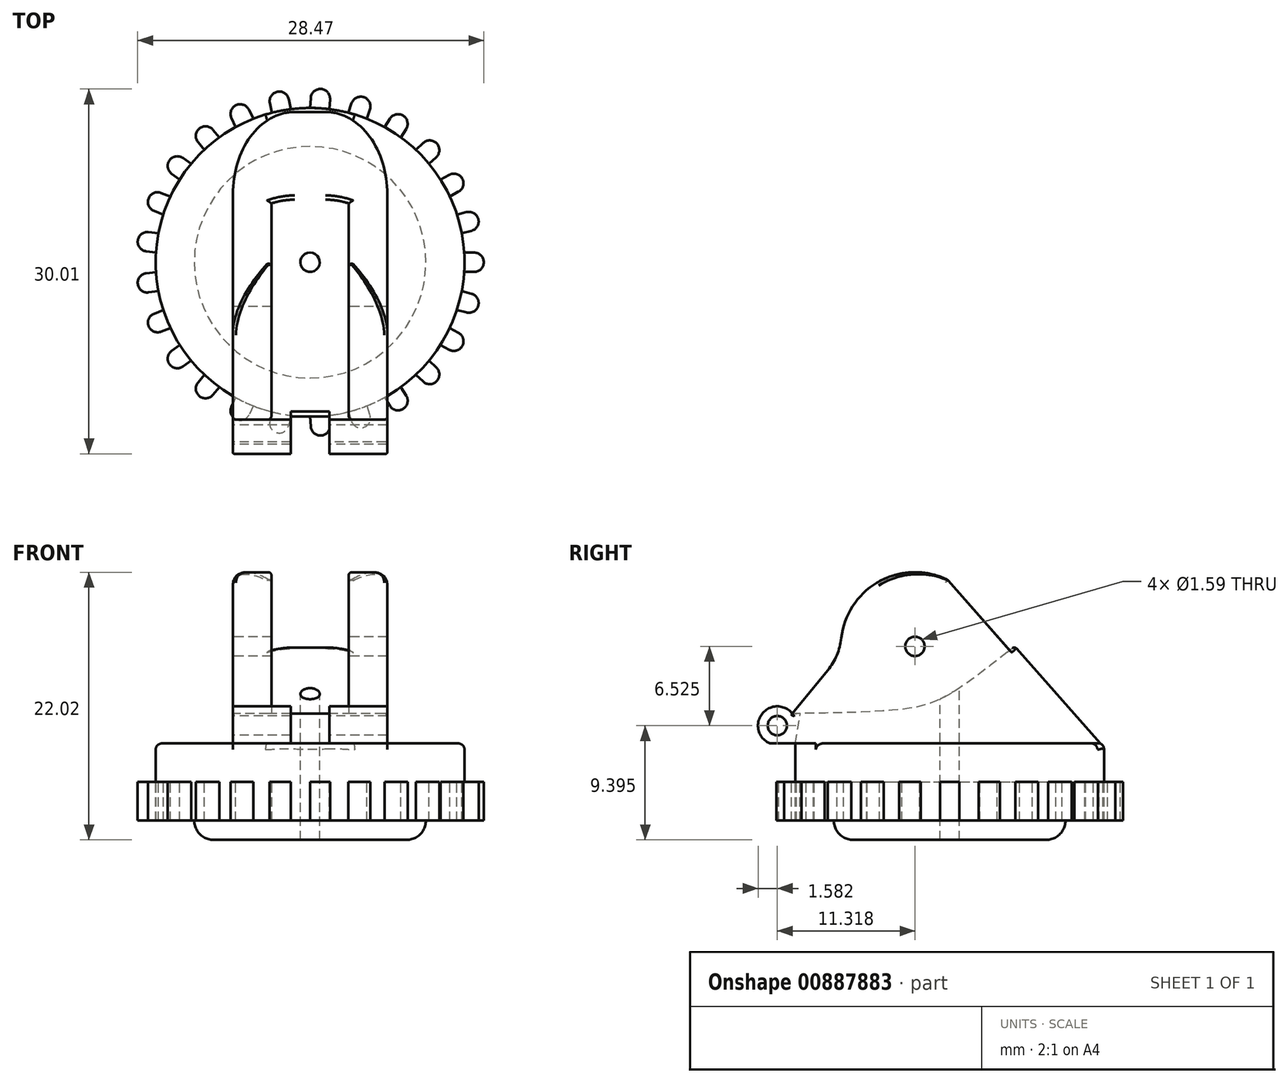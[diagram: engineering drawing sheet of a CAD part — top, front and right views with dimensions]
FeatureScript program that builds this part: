
annotation { "Feature Type Name" : "Feature", "Feature Type Description" : "" }
export const myFeature = defineFeature(function(context is Context, id is Id, definition is map)
    precondition{}
    {
        {
            var Q0;
            Q0=qCreatedBy(makeId("Right.planeOp"),FACE);
            var sketch = newSketch(context, id + "F0", { "sketchPlane" : qUnion([Q0])});
            skArc(sketch, "E0", {"start": v(4.53, 4.07) * mm, "mid": v(-2.46, 5.58) * mm, "end": v(-6.07, -0.6) * mm});
            skLineSegment(sketch, "E1", {"start": v(-6.07, -0.6) * mm, "end": v(-10.08, -5.53) * mm});
            skArc(sketch, "E2", {"start": v(-10.08, -5.53) * mm, "mid": v(-12.58, -5.57) * mm, "end": v(-11.94, -7.98) * mm});
            skCircle(sketch, "E3", {"center": v(0, 0) * mm, "radius": 0.8 * mm});
            skCircle(sketch, "E4", {"center": v(-11.32, -6.53) * mm, "radius": 0.8 * mm});
            skLineSegment(sketch, "E5", {"start": v(4.53, 4.07) * mm, "end": v(8.2, 0) * mm});
            skLineSegment(sketch, "E6", {"start": v(8.2, 0) * mm, "end": v(8.2, -7.98) * mm});
            skLineSegment(sketch, "E7", {"start": v(8.2, -7.98) * mm, "end": v(-11.94, -7.98) * mm});
            skPoint(sketch, "E8.end.orphan", {"position": v(0, -7.36) * mm});
            skFitSpline(sketch, "E9", {"points": [v(8.2, 0) * mm, v(2.56, -4.09) * mm, v(-1.11, -5.18) * mm, v(-10.08, -5.53) * mm], "startDerivative": vector(-17.3, -13.81) * mm, "endDerivative": vector(-25.55, -0.3) * mm});
            skLineSegment(sketch, "E10", {"start": v(-9.85, -7.98) * mm, "end": v(-9.42, -5.52) * mm});
            skLineSegment(sketch, "E11", {"start": v(8.2, 0) * mm, "end": v(15.23, -7.98) * mm});
            skLineSegment(sketch, "E12", {"start": v(15.23, -7.98) * mm, "end": v(8.2, -7.98) * mm});
            skSolve(sketch);
        }
        {
            var Q0;
            Q0=makeQuery(id+"F0.imprint","IMPRINT",FACE,{"disambiguationData":[TD([[makeQuery(id+"F0.imprint","IMPRINT",EDGE,{"derivedFrom":sQuery(id+"F0.wireOp",EDGE,"E0")}),1.0]])]});
            var Q1;
            {var subQ0=sQuery(id+"F0.wireOp",EDGE,"E6");Q1=makeQuery(id+"F0.imprint","IMPRINT",FACE,{"disambiguationData":[TD([[makeQuery(id+"F0.imprint","IMPRINT",EDGE,{"derivedFrom":subQ0}),-1.0]])]});}
            var Q2;
            {var subQ1=sQuery(id+"F0.wireOp",EDGE,"E2");Q2=makeQuery(id+"F0.imprint","IMPRINT",FACE,{"disambiguationData":[TD([[makeQuery(id+"F0.imprint","IMPRINT",EDGE,{"derivedFrom":subQ1}),1.0]])]});}
            extrude(context, id + "F1", {"entities" : qUnion([Q0, Q1, Q2]), "depth" : 12.7 * mm, "offsetDistance" : 25.4 * mm, "symmetric" : true});
        }
        {
            var Q0;
            Q0=makeQuery(id+"F0.imprint","IMPRINT",FACE,{"disambiguationData":[TD([[makeQuery(id+"F0.imprint","IMPRINT",EDGE,{"derivedFrom":sQuery(id+"F0.wireOp",EDGE,"E0")}),1.0]])]});
            extrude(context, id + "F2", {"entities" : qUnion([Q0]), "operationType" : NewBodyOperationType.REMOVE, "depth" : 6.35 * mm, "offsetDistance" : 25.4 * mm, "symmetric" : true});
        }
        {
            var Q0;
            {var subQ1=sQuery(id+"F0.wireOp",EDGE,"E2");Q0=makeQuery(id+"F0.imprint","IMPRINT",FACE,{"disambiguationData":[TD([[makeQuery(id+"F0.imprint","IMPRINT",EDGE,{"derivedFrom":subQ1}),1.0]])]});}
            extrude(context, id + "F3", {"entities" : qUnion([Q0]), "operationType" : NewBodyOperationType.REMOVE, "depth" : 3.17 * mm, "offsetDistance" : 25.4 * mm, "symmetric" : true});
        }
        {
            var Q0;
            Q0=makeQuery(id+"F1.opExtrude","SWEPT_FACE",FACE,{"disambiguationData":[OSD([sQuery(id+"F0.wireOp",EDGE,"E7")])]});
            var sketch = newSketch(context, id + "F4", { "sketchPlane" : qUnion([Q0])});
            skCircle(sketch, "E13", {"center": v(0, -2.85) * mm, "radius": 12.7 * mm});
            skPoint(sketch, "E13.centerSnap0", {"position": v(0, 9.85) * mm});
            skSolve(sketch);
        }
        {
            var Q0;
            {var subQ0=sQuery(id+"F0.wireOp",EDGE,"E7");var subQ2=makeQuery(id+"F1.opExtrude","SWEPT_EDGE",EDGE,{"disambiguationData":[OSD([sQuery(id+"F0.wireOp",EDGE,"E6"),subQ0])]});Q0=makeQuery(id+"F4.imprint","IMPRINT",FACE,{"disambiguationData":[TD([[makeQuery(id+"F4.imprint","IMPRINT",EDGE,{"derivedFrom":subQ2}),-1.0]])]});}
            var Q1;
            {var subQ1=sQuery(id+"F0.wireOp",EDGE,"E7");var subQ6=makeQuery(id+"F1.opExtrude","SWEPT_EDGE",EDGE,{"disambiguationData":[OSD([sQuery(id+"F0.wireOp",EDGE,"E6"),subQ1])]});Q1=makeQuery(id+"F4.imprint","IMPRINT",FACE,{"disambiguationData":[TD([[makeQuery(id+"F4.imprint","IMPRINT",EDGE,{"derivedFrom":subQ6}),1.0]])]});}
            extrude(context, id + "F5", {"entities" : qUnion([Q0, Q1]), "operationType" : NewBodyOperationType.ADD, "depth" : 3.17 * mm, "offsetDistance" : 25.4 * mm});
        }
        {
            var Q0;
            Q0=makeQuery(id+"F5.opExtrude","CAP_FACE",FACE,{"disambiguationData":[OSD([sQuery(id+"F4.wireOp",EDGE,"E13")])],"isStart":false});
            var sketch = newSketch(context, id + "F6", { "sketchPlane" : qUnion([Q0])});
            skCircle(sketch, "E14", {"center": v(0, -2.85) * mm, "radius": 12.7 * mm});
            skLineSegment(sketch, "E15", {"start": v(12.68, -2.06) * mm, "end": v(13.5, -2.06) * mm});
            skLineSegment(sketch, "E16", {"start": v(12.68, -3.65) * mm, "end": v(13.5, -3.65) * mm});
            skLineSegment(sketch, "E17", {"start": v(14.29, -2.85) * mm, "end": v(14.29, -2.85) * mm});
            skPoint(sketch, "E18.end.orphan", {"position": v(14.29, -2.85) * mm});
            skArc(sketch, "E19.filletArc", {"start": v(14.29, -2.85) * mm, "mid": v(14.06, -2.3) * mm, "end": v(13.5, -2.06) * mm});
            skArc(sketch, "E20.filletArc", {"start": v(13.5, -3.65) * mm, "mid": v(14.06, -3.42) * mm, "end": v(14.29, -2.85) * mm});
            skLineSegment(sketch, "E21.1.0", {"start": v(12.08, 1.07) * mm, "end": v(12.87, 1.27) * mm});
            skArc(sketch, "E21.1.1", {"start": v(13.84, 0.7) * mm, "mid": v(13.47, 1.18) * mm, "end": v(12.87, 1.27) * mm});
            skArc(sketch, "E21.1.2", {"start": v(13.27, -0.27) * mm, "mid": v(13.75, 0.1) * mm, "end": v(13.84, 0.7) * mm});
            skLineSegment(sketch, "E21.1.3", {"start": v(12.47, -0.47) * mm, "end": v(13.27, -0.27) * mm});
            skLineSegment(sketch, "E21.2.0", {"start": v(10.72, 3.95) * mm, "end": v(11.44, 4.34) * mm});
            skArc(sketch, "E21.2.1", {"start": v(12.52, 4.03) * mm, "mid": v(12.05, 4.4) * mm, "end": v(11.44, 4.34) * mm});
            skArc(sketch, "E21.2.2", {"start": v(12.2, 2.95) * mm, "mid": v(12.59, 3.43) * mm, "end": v(12.52, 4.03) * mm});
            skLineSegment(sketch, "E21.2.3", {"start": v(11.49, 2.56) * mm, "end": v(12.2, 2.95) * mm});
            skLineSegment(sketch, "E21.3.0", {"start": v(8.7, 6.4) * mm, "end": v(9.3, 6.96) * mm});
            skArc(sketch, "E21.3.1", {"start": v(10.42, 6.93) * mm, "mid": v(9.86, 7.18) * mm, "end": v(9.3, 6.96) * mm});
            skArc(sketch, "E21.3.2", {"start": v(10.38, 5.8) * mm, "mid": v(10.63, 6.36) * mm, "end": v(10.42, 6.93) * mm});
            skLineSegment(sketch, "E21.3.3", {"start": v(9.78, 5.24) * mm, "end": v(10.38, 5.8) * mm});
            skLineSegment(sketch, "E21.4.0", {"start": v(6.12, 8.27) * mm, "end": v(6.56, 8.96) * mm});
            skArc(sketch, "E21.4.1", {"start": v(7.66, 9.2) * mm, "mid": v(7.06, 9.31) * mm, "end": v(6.56, 8.96) * mm});
            skArc(sketch, "E21.4.2", {"start": v(7.9, 8.11) * mm, "mid": v(8, 8.71) * mm, "end": v(7.66, 9.2) * mm});
            skLineSegment(sketch, "E21.4.3", {"start": v(7.46, 7.42) * mm, "end": v(7.9, 8.11) * mm});
            skLineSegment(sketch, "E21.5.0", {"start": v(3.16, 9.45) * mm, "end": v(3.41, 10.22) * mm});
            skArc(sketch, "E21.5.1", {"start": v(4.42, 10.73) * mm, "mid": v(3.8, 10.69) * mm, "end": v(3.41, 10.22) * mm});
            skArc(sketch, "E21.5.2", {"start": v(4.92, 9.73) * mm, "mid": v(4.88, 10.34) * mm, "end": v(4.42, 10.73) * mm});
            skLineSegment(sketch, "E21.5.3", {"start": v(4.67, 8.96) * mm, "end": v(4.92, 9.73) * mm});
            skLineSegment(sketch, "E21.6.0", {"start": v(0, 9.85) * mm, "end": v(0.06, 10.66) * mm});
            skArc(sketch, "E21.6.1", {"start": v(0.9, 11.4) * mm, "mid": v(0.32, 11.2) * mm, "end": v(0.06, 10.66) * mm});
            skArc(sketch, "E21.6.2", {"start": v(1.64, 10.56) * mm, "mid": v(1.44, 11.14) * mm, "end": v(0.9, 11.4) * mm});
            skLineSegment(sketch, "E21.6.3", {"start": v(1.59, 9.75) * mm, "end": v(1.64, 10.56) * mm});
            skLineSegment(sketch, "E21.7.0", {"start": v(-3.15, 9.45) * mm, "end": v(-3.3, 10.25) * mm});
            skArc(sketch, "E21.7.1", {"start": v(-2.68, 11.18) * mm, "mid": v(-3.18, 10.85) * mm, "end": v(-3.3, 10.25) * mm});
            skArc(sketch, "E21.7.2", {"start": v(-1.75, 10.55) * mm, "mid": v(-2.08, 11.06) * mm, "end": v(-2.68, 11.18) * mm});
            skLineSegment(sketch, "E21.7.3", {"start": v(-1.6, 9.75) * mm, "end": v(-1.75, 10.55) * mm});
            skLineSegment(sketch, "E21.8.0", {"start": v(-6.12, 8.28) * mm, "end": v(-6.46, 9.02) * mm});
            skArc(sketch, "E21.8.1", {"start": v(-6.08, 10.07) * mm, "mid": v(-6.5, 9.62) * mm, "end": v(-6.46, 9.02) * mm});
            skArc(sketch, "E21.8.2", {"start": v(-5.03, 9.7) * mm, "mid": v(-5.48, 10.1) * mm, "end": v(-6.08, 10.07) * mm});
            skLineSegment(sketch, "E21.8.3", {"start": v(-4.68, 8.95) * mm, "end": v(-5.03, 9.7) * mm});
            skLineSegment(sketch, "E21.9.0", {"start": v(-8.7, 6.4) * mm, "end": v(-9.21, 7.04) * mm});
            skArc(sketch, "E21.9.1", {"start": v(-9.1, 8.15) * mm, "mid": v(-9.4, 7.62) * mm, "end": v(-9.21, 7.04) * mm});
            skArc(sketch, "E21.9.2", {"start": v(-7.99, 8.05) * mm, "mid": v(-8.53, 8.33) * mm, "end": v(-9.1, 8.15) * mm});
            skLineSegment(sketch, "E21.9.3", {"start": v(-7.47, 7.42) * mm, "end": v(-7.99, 8.05) * mm});
            skLineSegment(sketch, "E21.10.0", {"start": v(-10.72, 3.95) * mm, "end": v(-11.38, 4.44) * mm});
            skArc(sketch, "E21.10.1", {"start": v(-11.56, 5.54) * mm, "mid": v(-11.7, 4.95) * mm, "end": v(-11.38, 4.44) * mm});
            skArc(sketch, "E21.10.2", {"start": v(-10.45, 5.72) * mm, "mid": v(-11.04, 5.86) * mm, "end": v(-11.56, 5.54) * mm});
            skLineSegment(sketch, "E21.10.3", {"start": v(-9.79, 5.24) * mm, "end": v(-10.45, 5.72) * mm});
            skLineSegment(sketch, "E21.11.0", {"start": v(-12.08, 1.07) * mm, "end": v(-12.84, 1.38) * mm});
            skArc(sketch, "E21.11.1", {"start": v(-13.28, 2.4) * mm, "mid": v(-13.27, 1.8) * mm, "end": v(-12.84, 1.38) * mm});
            skArc(sketch, "E21.11.2", {"start": v(-12.25, 2.85) * mm, "mid": v(-12.86, 2.84) * mm, "end": v(-13.28, 2.4) * mm});
            skLineSegment(sketch, "E21.11.3", {"start": v(-11.5, 2.55) * mm, "end": v(-12.25, 2.85) * mm});
            skLineSegment(sketch, "E21.12.0", {"start": v(-12.67, -2.05) * mm, "end": v(-13.49, -1.95) * mm});
            skArc(sketch, "E21.12.1", {"start": v(-14.17, -1.06) * mm, "mid": v(-14.01, -1.65) * mm, "end": v(-13.49, -1.95) * mm});
            skArc(sketch, "E21.12.2", {"start": v(-13.29, -0.38) * mm, "mid": v(-13.87, -0.54) * mm, "end": v(-14.17, -1.06) * mm});
            skLineSegment(sketch, "E21.12.3", {"start": v(-12.48, -0.48) * mm, "end": v(-13.29, -0.38) * mm});
            skLineSegment(sketch, "E21.13.0", {"start": v(-12.48, -5.23) * mm, "end": v(-13.29, -5.33) * mm});
            skArc(sketch, "E21.13.1", {"start": v(-14.17, -4.64) * mm, "mid": v(-13.87, -5.17) * mm, "end": v(-13.29, -5.33) * mm});
            skArc(sketch, "E21.13.2", {"start": v(-13.49, -3.76) * mm, "mid": v(-14.01, -4.06) * mm, "end": v(-14.17, -4.64) * mm});
            skLineSegment(sketch, "E21.13.3", {"start": v(-12.67, -3.66) * mm, "end": v(-13.49, -3.76) * mm});
            skLineSegment(sketch, "E21.14.0", {"start": v(-11.5, -8.26) * mm, "end": v(-12.25, -8.56) * mm});
            skArc(sketch, "E21.14.1", {"start": v(-13.28, -8.11) * mm, "mid": v(-12.86, -8.55) * mm, "end": v(-12.25, -8.56) * mm});
            skArc(sketch, "E21.14.2", {"start": v(-12.84, -7.08) * mm, "mid": v(-13.27, -7.5) * mm, "end": v(-13.28, -8.11) * mm});
            skLineSegment(sketch, "E21.14.3", {"start": v(-12.08, -6.78) * mm, "end": v(-12.84, -7.08) * mm});
            skLineSegment(sketch, "E21.15.0", {"start": v(-9.79, -10.95) * mm, "end": v(-10.45, -11.43) * mm});
            skArc(sketch, "E21.15.1", {"start": v(-11.56, -11.25) * mm, "mid": v(-11.04, -11.57) * mm, "end": v(-10.45, -11.43) * mm});
            skArc(sketch, "E21.15.2", {"start": v(-11.38, -10.14) * mm, "mid": v(-11.7, -10.66) * mm, "end": v(-11.56, -11.25) * mm});
            skLineSegment(sketch, "E21.15.3", {"start": v(-10.72, -9.66) * mm, "end": v(-11.38, -10.14) * mm});
            skLineSegment(sketch, "E21.16.0", {"start": v(-7.47, -13.13) * mm, "end": v(-7.99, -13.76) * mm});
            skArc(sketch, "E21.16.1", {"start": v(-9.1, -13.86) * mm, "mid": v(-8.53, -14.04) * mm, "end": v(-7.99, -13.76) * mm});
            skArc(sketch, "E21.16.2", {"start": v(-9.21, -12.75) * mm, "mid": v(-9.4, -13.33) * mm, "end": v(-9.1, -13.86) * mm});
            skLineSegment(sketch, "E21.16.3", {"start": v(-8.7, -12.11) * mm, "end": v(-9.21, -12.75) * mm});
            skLineSegment(sketch, "E21.17.0", {"start": v(-4.68, -14.66) * mm, "end": v(-5.03, -15.4) * mm});
            skArc(sketch, "E21.17.1", {"start": v(-6.08, -15.78) * mm, "mid": v(-5.48, -15.81) * mm, "end": v(-5.03, -15.4) * mm});
            skArc(sketch, "E21.17.2", {"start": v(-6.46, -14.73) * mm, "mid": v(-6.5, -15.33) * mm, "end": v(-6.08, -15.78) * mm});
            skLineSegment(sketch, "E21.17.3", {"start": v(-6.12, -13.98) * mm, "end": v(-6.46, -14.73) * mm});
            skLineSegment(sketch, "E21.18.0", {"start": v(-1.6, -15.45) * mm, "end": v(-1.75, -16.26) * mm});
            skArc(sketch, "E21.18.1", {"start": v(-2.68, -16.89) * mm, "mid": v(-2.08, -16.77) * mm, "end": v(-1.75, -16.26) * mm});
            skArc(sketch, "E21.18.2", {"start": v(-3.3, -15.96) * mm, "mid": v(-3.18, -16.55) * mm, "end": v(-2.68, -16.89) * mm});
            skLineSegment(sketch, "E21.18.3", {"start": v(-3.15, -15.16) * mm, "end": v(-3.3, -15.96) * mm});
            skLineSegment(sketch, "E21.19.0", {"start": v(1.59, -15.45) * mm, "end": v(1.64, -16.27) * mm});
            skArc(sketch, "E21.19.1", {"start": v(0.9, -17.11) * mm, "mid": v(1.44, -16.85) * mm, "end": v(1.64, -16.27) * mm});
            skArc(sketch, "E21.19.2", {"start": v(0.06, -16.37) * mm, "mid": v(0.32, -16.92) * mm, "end": v(0.9, -17.11) * mm});
            skLineSegment(sketch, "E21.19.3", {"start": v(0, -15.55) * mm, "end": v(0.06, -16.37) * mm});
            skLineSegment(sketch, "E21.20.0", {"start": v(4.67, -14.66) * mm, "end": v(4.92, -15.44) * mm});
            skArc(sketch, "E21.20.1", {"start": v(4.42, -16.44) * mm, "mid": v(4.88, -16.05) * mm, "end": v(4.92, -15.44) * mm});
            skArc(sketch, "E21.20.2", {"start": v(3.41, -15.93) * mm, "mid": v(3.8, -16.4) * mm, "end": v(4.42, -16.44) * mm});
            skLineSegment(sketch, "E21.20.3", {"start": v(3.16, -15.15) * mm, "end": v(3.41, -15.93) * mm});
            skLineSegment(sketch, "E21.21.0", {"start": v(7.46, -13.13) * mm, "end": v(7.9, -13.82) * mm});
            skArc(sketch, "E21.21.1", {"start": v(7.66, -14.92) * mm, "mid": v(8, -14.42) * mm, "end": v(7.9, -13.82) * mm});
            skArc(sketch, "E21.21.2", {"start": v(6.56, -14.67) * mm, "mid": v(7.06, -15.02) * mm, "end": v(7.66, -14.92) * mm});
            skLineSegment(sketch, "E21.21.3", {"start": v(6.12, -13.98) * mm, "end": v(6.56, -14.67) * mm});
            skLineSegment(sketch, "E21.22.0", {"start": v(9.78, -10.95) * mm, "end": v(10.38, -11.51) * mm});
            skArc(sketch, "E21.22.1", {"start": v(10.42, -12.63) * mm, "mid": v(10.63, -12.07) * mm, "end": v(10.38, -11.51) * mm});
            skArc(sketch, "E21.22.2", {"start": v(9.3, -12.67) * mm, "mid": v(9.86, -12.88) * mm, "end": v(10.42, -12.63) * mm});
            skLineSegment(sketch, "E21.22.3", {"start": v(8.7, -12.1) * mm, "end": v(9.3, -12.67) * mm});
            skLineSegment(sketch, "E21.23.0", {"start": v(11.49, -8.26) * mm, "end": v(12.2, -8.66) * mm});
            skArc(sketch, "E21.23.1", {"start": v(12.52, -9.74) * mm, "mid": v(12.59, -9.13) * mm, "end": v(12.2, -8.66) * mm});
            skArc(sketch, "E21.23.2", {"start": v(11.44, -10.05) * mm, "mid": v(12.05, -10.12) * mm, "end": v(12.52, -9.74) * mm});
            skLineSegment(sketch, "E21.23.3", {"start": v(10.72, -9.66) * mm, "end": v(11.44, -10.05) * mm});
            skArc(sketch, "E22.3.24.0", {"start": v(13.84, -6.4) * mm, "mid": v(13.75, -5.8) * mm, "end": v(13.27, -5.44) * mm});
            skLineSegment(sketch, "E22.4.24.0", {"start": v(12.47, -5.24) * mm, "end": v(13.27, -5.44) * mm});
            skArc(sketch, "E22.7.24.0", {"start": v(12.87, -6.98) * mm, "mid": v(13.47, -6.9) * mm, "end": v(13.84, -6.4) * mm});
            skLineSegment(sketch, "E22.11.24.0", {"start": v(12.08, -6.77) * mm, "end": v(12.87, -6.98) * mm});
            skCircle(sketch, "E23", {"center": v(0, -2.85) * mm, "radius": 0.8 * mm});
            skCircle(sketch, "E24", {"center": v(0, -2.85) * mm, "radius": 9.53 * mm});
            skSolve(sketch);
        }
        {
            var Q0;
            {var subQ0=sQuery(id+"F6.wireOp",EDGE,"E21.18.0");Q0=makeQuery(id+"F6.imprint","IMPRINT",FACE,{"disambiguationData":[TD([[makeQuery(id+"F6.imprint","IMPRINT",EDGE,{"derivedFrom":subQ0}),-1.0]])]});}
            var Q1;
            {var subQ0=sQuery(id+"F6.wireOp",EDGE,"E21.17.0");Q1=makeQuery(id+"F6.imprint","IMPRINT",FACE,{"disambiguationData":[TD([[makeQuery(id+"F6.imprint","IMPRINT",EDGE,{"derivedFrom":subQ0}),-1.0]])]});}
            var Q2;
            {var subQ0=sQuery(id+"F6.wireOp",EDGE,"E21.16.0");Q2=makeQuery(id+"F6.imprint","IMPRINT",FACE,{"disambiguationData":[TD([[makeQuery(id+"F6.imprint","IMPRINT",EDGE,{"derivedFrom":subQ0}),-1.0]])]});}
            var Q3;
            {var subQ0=sQuery(id+"F6.wireOp",EDGE,"E21.15.0");Q3=makeQuery(id+"F6.imprint","IMPRINT",FACE,{"disambiguationData":[TD([[makeQuery(id+"F6.imprint","IMPRINT",EDGE,{"derivedFrom":subQ0}),-1.0]])]});}
            var Q4;
            {var subQ0=sQuery(id+"F6.wireOp",EDGE,"E21.14.0");Q4=makeQuery(id+"F6.imprint","IMPRINT",FACE,{"disambiguationData":[TD([[makeQuery(id+"F6.imprint","IMPRINT",EDGE,{"derivedFrom":subQ0}),-1.0]])]});}
            var Q5;
            Q5=makeQuery(id+"F6.imprint","IMPRINT",FACE,{"disambiguationData":[TD([[makeQuery(id+"F6.imprint","IMPRINT",EDGE,{"derivedFrom":sQuery(id+"F6.wireOp",EDGE,"E24")}),-1.0]])]});
            var Q6;
            {var subQ0=sQuery(id+"F6.wireOp",EDGE,"E21.13.0");Q6=makeQuery(id+"F6.imprint","IMPRINT",FACE,{"disambiguationData":[TD([[makeQuery(id+"F6.imprint","IMPRINT",EDGE,{"derivedFrom":subQ0}),-1.0]])]});}
            var Q7;
            {var subQ0=sQuery(id+"F6.wireOp",EDGE,"E21.12.0");Q7=makeQuery(id+"F6.imprint","IMPRINT",FACE,{"disambiguationData":[TD([[makeQuery(id+"F6.imprint","IMPRINT",EDGE,{"derivedFrom":subQ0}),-1.0]])]});}
            var Q8;
            {var subQ0=sQuery(id+"F6.wireOp",EDGE,"E21.11.0");Q8=makeQuery(id+"F6.imprint","IMPRINT",FACE,{"disambiguationData":[TD([[makeQuery(id+"F6.imprint","IMPRINT",EDGE,{"derivedFrom":subQ0}),-1.0]])]});}
            var Q9;
            {var subQ0=sQuery(id+"F6.wireOp",EDGE,"E21.10.0");Q9=makeQuery(id+"F6.imprint","IMPRINT",FACE,{"disambiguationData":[TD([[makeQuery(id+"F6.imprint","IMPRINT",EDGE,{"derivedFrom":subQ0}),-1.0]])]});}
            var Q10;
            {var subQ0=sQuery(id+"F6.wireOp",EDGE,"E21.9.0");Q10=makeQuery(id+"F6.imprint","IMPRINT",FACE,{"disambiguationData":[TD([[makeQuery(id+"F6.imprint","IMPRINT",EDGE,{"derivedFrom":subQ0}),-1.0]])]});}
            var Q11;
            {var subQ0=sQuery(id+"F6.wireOp",EDGE,"E21.8.0");Q11=makeQuery(id+"F6.imprint","IMPRINT",FACE,{"disambiguationData":[TD([[makeQuery(id+"F6.imprint","IMPRINT",EDGE,{"derivedFrom":subQ0}),-1.0]])]});}
            var Q12;
            {var subQ0=sQuery(id+"F6.wireOp",EDGE,"E21.7.0");Q12=makeQuery(id+"F6.imprint","IMPRINT",FACE,{"disambiguationData":[TD([[makeQuery(id+"F6.imprint","IMPRINT",EDGE,{"derivedFrom":subQ0}),-1.0]])]});}
            var Q13;
            {var subQ0=sQuery(id+"F6.wireOp",EDGE,"E21.6.0");Q13=makeQuery(id+"F6.imprint","IMPRINT",FACE,{"disambiguationData":[TD([[makeQuery(id+"F6.imprint","IMPRINT",EDGE,{"derivedFrom":subQ0}),-1.0]])]});}
            var Q14;
            {var subQ0=sQuery(id+"F6.wireOp",EDGE,"E21.5.0");Q14=makeQuery(id+"F6.imprint","IMPRINT",FACE,{"disambiguationData":[TD([[makeQuery(id+"F6.imprint","IMPRINT",EDGE,{"derivedFrom":subQ0}),-1.0]])]});}
            var Q15;
            {var subQ0=sQuery(id+"F6.wireOp",EDGE,"E21.4.0");Q15=makeQuery(id+"F6.imprint","IMPRINT",FACE,{"disambiguationData":[TD([[makeQuery(id+"F6.imprint","IMPRINT",EDGE,{"derivedFrom":subQ0}),-1.0]])]});}
            var Q16;
            {var subQ0=sQuery(id+"F6.wireOp",EDGE,"E21.3.0");Q16=makeQuery(id+"F6.imprint","IMPRINT",FACE,{"disambiguationData":[TD([[makeQuery(id+"F6.imprint","IMPRINT",EDGE,{"derivedFrom":subQ0}),-1.0]])]});}
            var Q17;
            {var subQ0=sQuery(id+"F6.wireOp",EDGE,"E21.2.0");Q17=makeQuery(id+"F6.imprint","IMPRINT",FACE,{"disambiguationData":[TD([[makeQuery(id+"F6.imprint","IMPRINT",EDGE,{"derivedFrom":subQ0}),-1.0]])]});}
            var Q18;
            {var subQ0=sQuery(id+"F6.wireOp",EDGE,"E21.1.0");Q18=makeQuery(id+"F6.imprint","IMPRINT",FACE,{"disambiguationData":[TD([[makeQuery(id+"F6.imprint","IMPRINT",EDGE,{"derivedFrom":subQ0}),-1.0]])]});}
            var Q19;
            {var subQ1=sQuery(id+"F6.wireOp",EDGE,"E15");Q19=makeQuery(id+"F6.imprint","IMPRINT",FACE,{"disambiguationData":[TD([[makeQuery(id+"F6.imprint","IMPRINT",EDGE,{"derivedFrom":subQ1}),-1.0]])]});}
            var Q20;
            Q20=makeQuery(id+"F6.imprint","IMPRINT",FACE,{"disambiguationData":[TD([[makeQuery(id+"F6.imprint","IMPRINT",EDGE,{"derivedFrom":sQuery(id+"F6.wireOp",EDGE,"E22.3.24.0")}),1.0]])]});
            var Q21;
            {var subQ0=sQuery(id+"F6.wireOp",EDGE,"E21.23.0");Q21=makeQuery(id+"F6.imprint","IMPRINT",FACE,{"disambiguationData":[TD([[makeQuery(id+"F6.imprint","IMPRINT",EDGE,{"derivedFrom":subQ0}),-1.0]])]});}
            var Q22;
            {var subQ0=sQuery(id+"F6.wireOp",EDGE,"E21.22.0");Q22=makeQuery(id+"F6.imprint","IMPRINT",FACE,{"disambiguationData":[TD([[makeQuery(id+"F6.imprint","IMPRINT",EDGE,{"derivedFrom":subQ0}),-1.0]])]});}
            var Q23;
            {var subQ0=sQuery(id+"F6.wireOp",EDGE,"E21.20.0");Q23=makeQuery(id+"F6.imprint","IMPRINT",FACE,{"disambiguationData":[TD([[makeQuery(id+"F6.imprint","IMPRINT",EDGE,{"derivedFrom":subQ0}),-1.0]])]});}
            var Q24;
            {var subQ0=sQuery(id+"F6.wireOp",EDGE,"E21.21.0");Q24=makeQuery(id+"F6.imprint","IMPRINT",FACE,{"disambiguationData":[TD([[makeQuery(id+"F6.imprint","IMPRINT",EDGE,{"derivedFrom":subQ0}),-1.0]])]});}
            var Q25;
            {var subQ0=sQuery(id+"F6.wireOp",EDGE,"E21.19.0");Q25=makeQuery(id+"F6.imprint","IMPRINT",FACE,{"disambiguationData":[TD([[makeQuery(id+"F6.imprint","IMPRINT",EDGE,{"derivedFrom":subQ0}),-1.0]])]});}
            extrude(context, id + "F7", {"entities" : qUnion([Q0, Q1, Q2, Q3, Q4, Q5, Q6, Q7, Q8, Q9, Q10, Q11, Q12, Q13, Q14, Q15, Q16, Q17, Q18, Q19, Q20, Q21, Q22, Q23, Q24, Q25]), "operationType" : NewBodyOperationType.ADD, "depth" : 3.17 * mm, "offsetDistance" : 25.4 * mm});
        }
        {
            var Q0;
            Q0=makeQuery(id+"F6.imprint","IMPRINT",FACE,{"disambiguationData":[TD([[makeQuery(id+"F6.imprint","IMPRINT",EDGE,{"derivedFrom":sQuery(id+"F6.wireOp",EDGE,"E23")}),-1.0]])]});
            extrude(context, id + "F8", {"entities" : qUnion([Q0]), "operationType" : NewBodyOperationType.ADD, "depth" : 4.76 * mm, "offsetDistance" : 25.4 * mm});
        }
        {
            var Q0;
            Q0=makeQuery(id+"F6.imprint","IMPRINT",FACE,{"disambiguationData":[TD([[makeQuery(id+"F6.imprint","IMPRINT",EDGE,{"derivedFrom":sQuery(id+"F6.wireOp",EDGE,"E23")}),1.0]])]});
            extrude(context, id + "F9", {"entities" : qUnion([Q0]), "operationType" : NewBodyOperationType.REMOVE, "oppositeDirection" : true, "depth" : 25.4 * mm, "offsetDistance" : 25.4 * mm});
        }
        {
            var Q0;
            Q0=makeQuery(id+"F0.imprint","IMPRINT",FACE,{"disambiguationData":[TD([[makeQuery(id+"F0.imprint","IMPRINT",EDGE,{"derivedFrom":sQuery(id+"F0.wireOp",EDGE,"E6")}),1.0]])]});
            extrude(context, id + "F10", {"entities" : qUnion([Q0]), "operationType" : NewBodyOperationType.ADD, "depth" : 12.7 * mm, "offsetDistance" : 25.4 * mm, "symmetric" : true});
        }
        {
            var Q0;
            Q0=makeQuery(id+"F10.opExtrude","CAP_EDGE",EDGE,{"disambiguationData":[OSD([sQuery(id+"F0.wireOp",EDGE,"E11")])],"isStart":true});
            var Q1;
            Q1=makeQuery(id+"F10.opExtrude","CAP_EDGE",EDGE,{"disambiguationData":[OSD([sQuery(id+"F0.wireOp",EDGE,"E11")])],"isStart":false});
            fillet(context, id + "F11", {"entities" : qUnion([Q0, Q1]), "radius" : 5.08 * mm, "tangentPropagation" : true, "allowEdgeOverflow" : false});
        }
        {
            var Q0;
            {var subQ0=sQuery(id+"F6.wireOp",EDGE,"E14");var subQ1=makeQuery(id+"F7.opExtrude","SWEPT_FACE",FACE,{"disambiguationData":[OSD([subQ0]),TDD([makeQuery(id+"F6.imprint","IMPRINT",EDGE,{"disambiguationData":[TD([[makeQuery(id+"F6.imprint","INTERSECT",VERTEX,{"derivedFrom":[subQ0,sQuery(id+"F6.wireOp",EDGE,"E21.19.0")]}),-1.0]])],"derivedFrom":subQ0})])]});var subQ2=makeQuery(id+"F7.opExtrude","SWEPT_FACE",FACE,{"disambiguationData":[OSD([subQ0]),TDD([makeQuery(id+"F6.imprint","IMPRINT",EDGE,{"disambiguationData":[TD([[makeQuery(id+"F6.imprint","INTERSECT",VERTEX,{"derivedFrom":[subQ0,sQuery(id+"F6.wireOp",EDGE,"E21.18.0")]}),-1.0]])],"derivedFrom":subQ0})])]});var subQ3=makeQuery(id+"F7.opExtrude","SWEPT_FACE",FACE,{"disambiguationData":[OSD([subQ0]),TDD([makeQuery(id+"F6.imprint","IMPRINT",EDGE,{"disambiguationData":[TD([[makeQuery(id+"F6.imprint","INTERSECT",VERTEX,{"derivedFrom":[subQ0,sQuery(id+"F6.wireOp",EDGE,"E21.17.0")]}),-1.0]])],"derivedFrom":subQ0})])]});var subQ4=makeQuery(id+"F7.opExtrude","SWEPT_FACE",FACE,{"disambiguationData":[OSD([subQ0]),TDD([makeQuery(id+"F6.imprint","IMPRINT",EDGE,{"disambiguationData":[TD([[makeQuery(id+"F6.imprint","INTERSECT",VERTEX,{"derivedFrom":[subQ0,sQuery(id+"F6.wireOp",EDGE,"E21.16.0")]}),-1.0]])],"derivedFrom":subQ0})])]});var subQ5=makeQuery(id+"F7.opExtrude","SWEPT_FACE",FACE,{"disambiguationData":[OSD([subQ0]),TDD([makeQuery(id+"F6.imprint","IMPRINT",EDGE,{"disambiguationData":[TD([[makeQuery(id+"F6.imprint","INTERSECT",VERTEX,{"derivedFrom":[subQ0,sQuery(id+"F6.wireOp",EDGE,"E21.15.0")]}),-1.0]])],"derivedFrom":subQ0})])]});var subQ6=makeQuery(id+"F7.opExtrude","SWEPT_FACE",FACE,{"disambiguationData":[OSD([subQ0]),TDD([makeQuery(id+"F6.imprint","IMPRINT",EDGE,{"disambiguationData":[TD([[makeQuery(id+"F6.imprint","INTERSECT",VERTEX,{"derivedFrom":[subQ0,sQuery(id+"F6.wireOp",EDGE,"E21.14.0")]}),-1.0]])],"derivedFrom":subQ0})])]});var subQ7=makeQuery(id+"F7.opExtrude","SWEPT_FACE",FACE,{"disambiguationData":[OSD([subQ0]),TDD([makeQuery(id+"F6.imprint","IMPRINT",EDGE,{"disambiguationData":[TD([[makeQuery(id+"F6.imprint","INTERSECT",VERTEX,{"derivedFrom":[subQ0,sQuery(id+"F6.wireOp",EDGE,"E21.13.0")]}),-1.0]])],"derivedFrom":subQ0})])]});var subQ8=makeQuery(id+"F7.opExtrude","SWEPT_FACE",FACE,{"disambiguationData":[OSD([subQ0]),TDD([makeQuery(id+"F6.imprint","IMPRINT",EDGE,{"disambiguationData":[TD([[makeQuery(id+"F6.imprint","INTERSECT",VERTEX,{"derivedFrom":[subQ0,sQuery(id+"F6.wireOp",EDGE,"E21.12.0")]}),-1.0]])],"derivedFrom":subQ0})])]});var subQ9=makeQuery(id+"F7.opExtrude","SWEPT_FACE",FACE,{"disambiguationData":[OSD([subQ0]),TDD([makeQuery(id+"F6.imprint","IMPRINT",EDGE,{"disambiguationData":[TD([[makeQuery(id+"F6.imprint","INTERSECT",VERTEX,{"derivedFrom":[subQ0,sQuery(id+"F6.wireOp",EDGE,"E21.11.0")]}),-1.0]])],"derivedFrom":subQ0})])]});var subQ10=sQuery(id+"F0.wireOp",EDGE,"E12");var subQ12=makeQuery(id+"F7.opExtrude","SWEPT_FACE",FACE,{"disambiguationData":[OSD([subQ0]),TDD([makeQuery(id+"F6.imprint","IMPRINT",EDGE,{"disambiguationData":[TD([[makeQuery(id+"F6.imprint","INTERSECT",VERTEX,{"derivedFrom":[subQ0,sQuery(id+"F6.wireOp",EDGE,"E21.10.0")]}),-1.0]])],"derivedFrom":subQ0})])]});var subQ13=sQuery(id+"F0.wireOp",EDGE,"E11");var subQ14=makeQuery(id+"F7.opExtrude","SWEPT_FACE",FACE,{"disambiguationData":[OSD([subQ0]),TDD([makeQuery(id+"F6.imprint","IMPRINT",EDGE,{"disambiguationData":[TD([[makeQuery(id+"F6.imprint","INTERSECT",VERTEX,{"derivedFrom":[subQ0,sQuery(id+"F6.wireOp",EDGE,"E21.1.0")]}),-1.0]])],"derivedFrom":subQ0})])]});var subQ15=makeQuery(id+"F7.opExtrude","SWEPT_FACE",FACE,{"disambiguationData":[OSD([subQ0]),TDD([makeQuery(id+"F6.imprint","IMPRINT",EDGE,{"disambiguationData":[TD([[makeQuery(id+"F6.imprint","INTERSECT",VERTEX,{"derivedFrom":[subQ0,sQuery(id+"F6.wireOp",EDGE,"E15")]}),-1.0]])],"derivedFrom":subQ0})])]});var subQ16=makeQuery(id+"F7.opExtrude","SWEPT_FACE",FACE,{"disambiguationData":[OSD([subQ0]),TDD([makeQuery(id+"F6.imprint","IMPRINT",EDGE,{"disambiguationData":[TD([[makeQuery(id+"F6.imprint","INTERSECT",VERTEX,{"derivedFrom":[subQ0,sQuery(id+"F6.wireOp",EDGE,"E21.9.0")]}),-1.0]])],"derivedFrom":subQ0})])]});var subQ17=sQuery(id+"F4.wireOp",EDGE,"E13");var subQ18=makeQuery(id+"F5.opExtrude","CAP_FACE",FACE,{"disambiguationData":[OSD([subQ17])],"isStart":true});var subQ19=makeQuery(id+"F7.opExtrude","SWEPT_FACE",FACE,{"disambiguationData":[OSD([subQ0]),TDD([makeQuery(id+"F6.imprint","IMPRINT",EDGE,{"disambiguationData":[TD([[makeQuery(id+"F6.imprint","INTERSECT",VERTEX,{"derivedFrom":[subQ0,sQuery(id+"F6.wireOp",EDGE,"E21.5.0")]}),-1.0]])],"derivedFrom":subQ0})])]});var subQ20=makeQuery(id+"F7.opExtrude","SWEPT_FACE",FACE,{"disambiguationData":[OSD([subQ0]),TDD([makeQuery(id+"F6.imprint","IMPRINT",EDGE,{"disambiguationData":[TD([[makeQuery(id+"F6.imprint","INTERSECT",VERTEX,{"derivedFrom":[subQ0,sQuery(id+"F6.wireOp",EDGE,"E21.8.0")]}),-1.0]])],"derivedFrom":subQ0})])]});var subQ21=makeQuery(id+"F5.opExtrude","SWEPT_FACE",FACE,{"disambiguationData":[OSD([subQ17])]});var subQ22=makeQuery(id+"F7.opExtrude","SWEPT_FACE",FACE,{"disambiguationData":[OSD([subQ0]),TDD([makeQuery(id+"F6.imprint","IMPRINT",EDGE,{"disambiguationData":[TD([[makeQuery(id+"F6.imprint","INTERSECT",VERTEX,{"derivedFrom":[subQ0,sQuery(id+"F6.wireOp",EDGE,"E21.4.0")]}),-1.0]])],"derivedFrom":subQ0})])]});var subQ23=makeQuery(id+"F7.opExtrude","SWEPT_FACE",FACE,{"disambiguationData":[OSD([subQ0]),TDD([makeQuery(id+"F6.imprint","IMPRINT",EDGE,{"disambiguationData":[TD([[makeQuery(id+"F6.imprint","INTERSECT",VERTEX,{"derivedFrom":[subQ0,sQuery(id+"F6.wireOp",EDGE,"E21.2.0")]}),-1.0]])],"derivedFrom":subQ0})])]});var subQ24=makeQuery(id+"F7.opExtrude","SWEPT_FACE",FACE,{"disambiguationData":[OSD([subQ0]),TDD([makeQuery(id+"F6.imprint","IMPRINT",EDGE,{"disambiguationData":[TD([[makeQuery(id+"F6.imprint","INTERSECT",VERTEX,{"derivedFrom":[subQ0,sQuery(id+"F6.wireOp",EDGE,"E21.3.0")]}),-1.0]])],"derivedFrom":subQ0})])]});var subQ25=makeQuery(id+"F7.opExtrude","SWEPT_FACE",FACE,{"disambiguationData":[OSD([subQ0]),TDD([makeQuery(id+"F6.imprint","IMPRINT",EDGE,{"disambiguationData":[TD([[makeQuery(id+"F6.imprint","INTERSECT",VERTEX,{"derivedFrom":[subQ0,sQuery(id+"F6.wireOp",EDGE,"E21.6.0")]}),-1.0]])],"derivedFrom":subQ0})])]});var subQ26=makeQuery(id+"F7.opExtrude","SWEPT_FACE",FACE,{"disambiguationData":[OSD([subQ0]),TDD([makeQuery(id+"F6.imprint","IMPRINT",EDGE,{"disambiguationData":[TD([[makeQuery(id+"F6.imprint","INTERSECT",VERTEX,{"derivedFrom":[subQ0,sQuery(id+"F6.wireOp",EDGE,"E21.7.0")]}),-1.0]])],"derivedFrom":subQ0})])]});var subQ27=makeQuery(id+"F7.opExtrude","SWEPT_FACE",FACE,{"disambiguationData":[OSD([subQ0]),TDD([makeQuery(id+"F6.imprint","IMPRINT",EDGE,{"disambiguationData":[TD([[makeQuery(id+"F6.imprint","INTERSECT",VERTEX,{"derivedFrom":[subQ0,sQuery(id+"F6.wireOp",EDGE,"E21.20.0")]}),-1.0]])],"derivedFrom":subQ0})])]});var subQ28=makeQuery(id+"F7.opExtrude","SWEPT_FACE",FACE,{"disambiguationData":[OSD([subQ0]),TDD([makeQuery(id+"F6.imprint","IMPRINT",EDGE,{"disambiguationData":[TD([[makeQuery(id+"F6.imprint","INTERSECT",VERTEX,{"derivedFrom":[subQ0,sQuery(id+"F6.wireOp",EDGE,"E21.21.0")]}),-1.0]])],"derivedFrom":subQ0})])]});var subQ29=makeQuery(id+"F7.opExtrude","SWEPT_FACE",FACE,{"disambiguationData":[OSD([subQ0]),TDD([makeQuery(id+"F6.imprint","IMPRINT",EDGE,{"disambiguationData":[TD([[makeQuery(id+"F6.imprint","INTERSECT",VERTEX,{"derivedFrom":[subQ0,sQuery(id+"F6.wireOp",EDGE,"E21.22.0")]}),-1.0]])],"derivedFrom":subQ0})])]});var subQ30=makeQuery(id+"F7.opExtrude","SWEPT_FACE",FACE,{"disambiguationData":[OSD([subQ0]),TDD([makeQuery(id+"F6.imprint","IMPRINT",EDGE,{"disambiguationData":[TD([[makeQuery(id+"F6.imprint","INTERSECT",VERTEX,{"derivedFrom":[subQ0,sQuery(id+"F6.wireOp",EDGE,"E21.23.0")]}),-1.0]])],"derivedFrom":subQ0})])]});var subQ31=makeQuery(id+"F7.opExtrude","SWEPT_FACE",FACE,{"disambiguationData":[OSD([subQ0]),TDD([makeQuery(id+"F6.imprint","IMPRINT",EDGE,{"disambiguationData":[TD([[makeQuery(id+"F6.imprint","INTERSECT",VERTEX,{"derivedFrom":[subQ0,sQuery(id+"F6.wireOp",EDGE,"E16")]}),1.0]])],"derivedFrom":subQ0})])]});var subQ32=makeQuery(id+"F5.boolean.opBoolean","SPLIT",EDGE,{"disambiguationData":[topologyDisambiguationEdgeConnected([subQ21,subQ18])],"derivedFrom":makeQuery(id+"F5.opExtrude","CAP_EDGE",EDGE,{"disambiguationData":[OSD([subQ17])],"isStart":true})});var subQ35=sQuery(id+"F0.wireOp",EDGE,"E6");Q0=makeQuery(id+"F11.opFillet","MERGE",EDGE,{"derivedFrom":[makeQuery(id+"F10.boolean.opBoolean","SPLIT",EDGE,{"disambiguationData":[topologyDisambiguationEdgeConnected([subQ21,subQ18,subQ15,subQ14,subQ23,subQ24,subQ22,subQ19,subQ25,subQ26,subQ20,subQ16,subQ12,subQ9,subQ8,subQ7,subQ6,subQ5,subQ4,subQ3,subQ2,subQ1,subQ27,subQ28,subQ29,subQ30,subQ31]),TD([makeQuery(id+"F10.opExtrude","CAP_FACE",FACE,{"disambiguationData":[OSD([subQ35,subQ13,subQ10])],"isStart":true})])],"derivedFrom":subQ32}),makeQuery(id+"F10.boolean.opBoolean","SPLIT",EDGE,{"disambiguationData":[topologyDisambiguationEdgeConnected([subQ21,subQ18,subQ15,subQ14,subQ23,subQ24,subQ22,subQ19,subQ25,subQ26,subQ20,subQ16,subQ12,subQ9,subQ8,subQ7,subQ6,subQ5,subQ4,subQ3,subQ2,subQ1,subQ27,subQ28,subQ29,subQ30,subQ31]),TD([makeQuery(id+"F10.opExtrude","CAP_FACE",FACE,{"disambiguationData":[OSD([subQ35,subQ13,subQ10])],"isStart":false})])],"derivedFrom":subQ32}),makeQuery(id+"F10.boolean.opBoolean","SPLIT",EDGE,{"disambiguationData":[topologyDisambiguationEdgeConnected([subQ21,subQ18,subQ15,subQ14,subQ23,subQ24,subQ22,subQ19,subQ25,subQ26,subQ20,subQ16,subQ12,subQ9,subQ8,subQ7,subQ6,subQ5,subQ4,subQ3,subQ2,subQ1,subQ27,subQ28,subQ29,subQ30,subQ31]),TD([makeQuery(id+"F10.opExtrude","SWEPT_FACE",FACE,{"disambiguationData":[OSD([subQ13])]})])],"derivedFrom":subQ32})]});}
            fillet(context, id + "F12", {"entities" : qUnion([Q0]), "radius" : 0.5 * mm, "tangentPropagation" : true, "allowEdgeOverflow" : false});
        }
        {
            var Q0;
            Q0=makeQuery(id+"F8.opExtrude","CAP_EDGE",EDGE,{"disambiguationData":[OSD([sQuery(id+"F6.wireOp",EDGE,"E24")])],"isStart":false});
            fillet(context, id + "F13", {"entities" : qUnion([Q0]), "radius" : 1.59 * mm, "tangentPropagation" : true, "allowEdgeOverflow" : false});
        }
        {
            var Q0;
            {var subQ0=sQuery(id+"F0.wireOp",EDGE,"E0");var subQ1=sQuery(id+"F0.wireOp",EDGE,"E5");var subQ2=sQuery(id+"F0.wireOp",EDGE,"E3");var subQ3=sQuery(id+"F0.wireOp",EDGE,"E1");Q0=makeQuery(id+"F2.boolean.opBoolean","SPLIT",EDGE,{"disambiguationData":[TD([makeQuery(id+"F2.opExtrude","CAP_FACE",FACE,{"disambiguationData":[OSD([subQ0,subQ3,subQ2,subQ1,sQuery(id+"F0.wireOp",EDGE,"E9")])],"isStart":false})])],"derivedFrom":makeQuery(id+"F1.opExtrude","SWEPT_EDGE",EDGE,{"disambiguationData":[OSD([subQ0,subQ3])]})});}
            var Q1;
            {var subQ0=sQuery(id+"F0.wireOp",EDGE,"E0");var subQ1=sQuery(id+"F0.wireOp",EDGE,"E5");var subQ2=sQuery(id+"F0.wireOp",EDGE,"E3");var subQ3=sQuery(id+"F0.wireOp",EDGE,"E1");Q1=makeQuery(id+"F2.boolean.opBoolean","SPLIT",EDGE,{"disambiguationData":[TD([makeQuery(id+"F2.opExtrude","CAP_FACE",FACE,{"disambiguationData":[OSD([subQ0,subQ3,subQ2,subQ1,sQuery(id+"F0.wireOp",EDGE,"E9")])],"isStart":true})])],"derivedFrom":makeQuery(id+"F1.opExtrude","SWEPT_EDGE",EDGE,{"disambiguationData":[OSD([subQ0,subQ3])]})});}
            fillet(context, id + "F14", {"entities" : qUnion([Q0, Q1]), "radius" : 5.08 * mm, "tangentPropagation" : true, "allowEdgeOverflow" : false});
        }
        {
            var Q0;
            {var subQ0=sQuery(id+"F0.wireOp",EDGE,"E5");var subQ1=sQuery(id+"F0.wireOp",EDGE,"E3");var subQ2=sQuery(id+"F0.wireOp",EDGE,"E1");var subQ3=sQuery(id+"F0.wireOp",EDGE,"E0");Q0=makeQuery(id+"F2.boolean.opBoolean","SPLIT",FACE,{"disambiguationData":[TD([makeQuery(id+"F2.opExtrude","CAP_FACE",FACE,{"disambiguationData":[OSD([subQ3,subQ2,subQ1,subQ0,sQuery(id+"F0.wireOp",EDGE,"E9")])],"isStart":false})])],"derivedFrom":makeQuery(id+"F1.opExtrude","SWEPT_FACE",FACE,{"disambiguationData":[OSD([subQ3])]})});}
            var Q1;
            {var subQ0=sQuery(id+"F0.wireOp",EDGE,"E5");var subQ1=sQuery(id+"F0.wireOp",EDGE,"E3");var subQ2=sQuery(id+"F0.wireOp",EDGE,"E1");var subQ3=sQuery(id+"F0.wireOp",EDGE,"E0");Q1=makeQuery(id+"F2.boolean.opBoolean","SPLIT",FACE,{"disambiguationData":[TD([makeQuery(id+"F2.opExtrude","CAP_FACE",FACE,{"disambiguationData":[OSD([subQ3,subQ2,subQ1,subQ0,sQuery(id+"F0.wireOp",EDGE,"E9")])],"isStart":true})])],"derivedFrom":makeQuery(id+"F1.opExtrude","SWEPT_FACE",FACE,{"disambiguationData":[OSD([subQ3])]})});}
            fillet(context, id + "F15", {"entities" : qUnion([Q0, Q1]), "radius" : 0.25 * mm, "tangentPropagation" : true, "allowEdgeOverflow" : false});
        }
        {
            var Q0;
            Q0=makeQuery(id+"F3.boolean.opBoolean","COPY",EDGE,{"derivedFrom":makeQuery(id+"F3.opExtrude","CAP_EDGE",EDGE,{"disambiguationData":[OSD([sQuery(id+"F0.wireOp",EDGE,"E2")])],"isStart":false})});
            var Q1;
            Q1=makeQuery(id+"F3.boolean.opBoolean","COPY",EDGE,{"derivedFrom":makeQuery(id+"F3.opExtrude","CAP_EDGE",EDGE,{"disambiguationData":[OSD([sQuery(id+"F0.wireOp",EDGE,"E2")])],"isStart":true})});
            var Q2;
            Q2=makeQuery(id+"F1.opExtrude","CAP_EDGE",EDGE,{"disambiguationData":[OSD([sQuery(id+"F0.wireOp",EDGE,"E2")])],"isStart":true});
            var Q3;
            Q3=makeQuery(id+"F1.opExtrude","CAP_EDGE",EDGE,{"disambiguationData":[OSD([sQuery(id+"F0.wireOp",EDGE,"E2")])],"isStart":false});
            fillet(context, id + "F16", {"entities" : qUnion([Q0, Q1, Q2, Q3]), "radius" : 0.13 * mm, "tangentPropagation" : true, "allowEdgeOverflow" : false});
        }
        {
            var Q0;
            Q0=makeQuery(id+"F11.opFillet","BLEND_EDGE",EDGE,{"blendedFrom":[makeQuery(id+"F10.opExtrude","CAP_EDGE",EDGE,{"disambiguationData":[OSD([sQuery(id+"F0.wireOp",EDGE,"E11")])],"isStart":true}),makeQuery(id+"F2.boolean.opBoolean","COPY",FACE,{"derivedFrom":makeQuery(id+"F2.opExtrude","CAP_FACE",FACE,{"disambiguationData":[OSD([sQuery(id+"F0.wireOp",EDGE,"E0"),sQuery(id+"F0.wireOp",EDGE,"E1"),sQuery(id+"F0.wireOp",EDGE,"E3"),sQuery(id+"F0.wireOp",EDGE,"E5"),sQuery(id+"F0.wireOp",EDGE,"E9")])],"isStart":true})})],"blendedInto":[makeQuery(id+"F2.boolean.opBoolean","COPY",FACE,{"derivedFrom":makeQuery(id+"F2.opExtrude","CAP_FACE",FACE,{"disambiguationData":[OSD([sQuery(id+"F0.wireOp",EDGE,"E0"),sQuery(id+"F0.wireOp",EDGE,"E1"),sQuery(id+"F0.wireOp",EDGE,"E3"),sQuery(id+"F0.wireOp",EDGE,"E5"),sQuery(id+"F0.wireOp",EDGE,"E9")])],"isStart":true})})]});
            var Q1;
            Q1=makeQuery(id+"F11.opFillet","BLEND_EDGE",EDGE,{"blendedFrom":[makeQuery(id+"F10.opExtrude","CAP_EDGE",EDGE,{"disambiguationData":[OSD([sQuery(id+"F0.wireOp",EDGE,"E11")])],"isStart":false}),makeQuery(id+"F2.boolean.opBoolean","COPY",FACE,{"derivedFrom":makeQuery(id+"F2.opExtrude","CAP_FACE",FACE,{"disambiguationData":[OSD([sQuery(id+"F0.wireOp",EDGE,"E0"),sQuery(id+"F0.wireOp",EDGE,"E1"),sQuery(id+"F0.wireOp",EDGE,"E3"),sQuery(id+"F0.wireOp",EDGE,"E5"),sQuery(id+"F0.wireOp",EDGE,"E9")])],"isStart":false})})],"blendedInto":[makeQuery(id+"F2.boolean.opBoolean","COPY",FACE,{"derivedFrom":makeQuery(id+"F2.opExtrude","CAP_FACE",FACE,{"disambiguationData":[OSD([sQuery(id+"F0.wireOp",EDGE,"E0"),sQuery(id+"F0.wireOp",EDGE,"E1"),sQuery(id+"F0.wireOp",EDGE,"E3"),sQuery(id+"F0.wireOp",EDGE,"E5"),sQuery(id+"F0.wireOp",EDGE,"E9")])],"isStart":false})})]});
            fillet(context, id + "F17", {"entities" : qUnion([Q0, Q1]), "radius" : 0.25 * mm, "tangentPropagation" : true, "allowEdgeOverflow" : false});
        }
        {
            var Q0;
            Q0=makeQuery(id+"F11.opFillet","BLEND_EDGE",EDGE,{"blendedFrom":[makeQuery(id+"F10.opExtrude","CAP_EDGE",EDGE,{"disambiguationData":[OSD([sQuery(id+"F0.wireOp",EDGE,"E11")])],"isStart":false}),makeQuery(id+"F2.boolean.opBoolean","COPY",FACE,{"derivedFrom":makeQuery(id+"F2.opExtrude","SWEPT_FACE",FACE,{"disambiguationData":[OSD([sQuery(id+"F0.wireOp",EDGE,"E9")])]})})],"blendedInto":[makeQuery(id+"F2.boolean.opBoolean","COPY",FACE,{"derivedFrom":makeQuery(id+"F2.opExtrude","SWEPT_FACE",FACE,{"disambiguationData":[OSD([sQuery(id+"F0.wireOp",EDGE,"E9")])]})})]});
            var Q1;
            {var subQ0=sQuery(id+"F0.wireOp",EDGE,"E11");var subQ1=sQuery(id+"F0.wireOp",EDGE,"E9");var subQ2=sQuery(id+"F0.wireOp",EDGE,"E6");var subQ3=sQuery(id+"F0.wireOp",EDGE,"E5");Q1=makeQuery(id+"F10.boolean.opBoolean","MERGE",EDGE,{"derivedFrom":[makeQuery(id+"F2.boolean.opBoolean","MERGE",EDGE,{"derivedFrom":[makeQuery(id+"F1.opExtrude","SWEPT_EDGE",EDGE,{"disambiguationData":[OSD([subQ3,subQ2,subQ1,subQ0])]})],"fromTools":[makeQuery(id+"F2.opExtrude","SWEPT_EDGE",EDGE,{"disambiguationData":[OSD([subQ3,subQ2,subQ1,subQ0])]})]}),makeQuery(id+"F10.opExtrude","SWEPT_EDGE",EDGE,{"disambiguationData":[OSD([subQ3,subQ2,subQ1,subQ0])]})]});}
            var Q2;
            Q2=makeQuery(id+"F11.opFillet","BLEND_EDGE",EDGE,{"blendedFrom":[makeQuery(id+"F10.opExtrude","CAP_EDGE",EDGE,{"disambiguationData":[OSD([sQuery(id+"F0.wireOp",EDGE,"E11")])],"isStart":true}),makeQuery(id+"F2.boolean.opBoolean","COPY",FACE,{"derivedFrom":makeQuery(id+"F2.opExtrude","SWEPT_FACE",FACE,{"disambiguationData":[OSD([sQuery(id+"F0.wireOp",EDGE,"E9")])]})})],"blendedInto":[makeQuery(id+"F2.boolean.opBoolean","COPY",FACE,{"derivedFrom":makeQuery(id+"F2.opExtrude","SWEPT_FACE",FACE,{"disambiguationData":[OSD([sQuery(id+"F0.wireOp",EDGE,"E9")])]})})]});
            fillet(context, id + "F18", {"entities" : qUnion([Q0, Q1, Q2]), "radius" : 0.25 * mm, "tangentPropagation" : true, "allowEdgeOverflow" : false});
        }
    });
